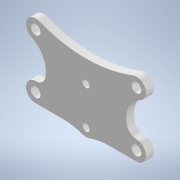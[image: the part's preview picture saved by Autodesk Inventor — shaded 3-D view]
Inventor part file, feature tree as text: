
AUTODESK INVENTOR PART (.ipt)
format: ipt  version: 2022 (Build 260153070, 153G)  size: 151,552 bytes
history: native  units: mm
features: reference x17, other x4, extrude x1, sketch x1
ambient origin geometry x8: Origin, YZ Plane, XZ Plane, XY Plane, X Axis, Y Axis, Z Axis, Center Point
bodies: Solid1 (feature_tree)
feature tree (23):
  extrude  "Extrusion1"  Depth=2.5mm
  sketch  "Sketch1"  dims[d0=1.5mm d1=15.0mm d2=2.5mm d3=0.0mm]
  reference  "Reference1"
  reference  "Reference2"
  reference  "Reference3"
  reference  "Reference4"
  reference  "Reference5"
  reference  "Reference6"
  reference  "Reference7"
  reference  "Reference8"
  reference  "Reference9"
  reference  "Reference10"
  reference  "Reference11"
  reference  "Reference12"
  reference  "Reference13"
  reference  "Reference14"
  reference  "Reference15"
  reference  "Reference16"
  reference  "Reference17"
  other  "<userpath> laptop\Desktop\SumoBot\sumobotLIDAR\sumobotLIDAR.iam"
  other  "sumobotLIDAR.iam"
  other  "AS5600:1"
  other  "Adapterlowerplate:1"
